# Revit family: FEVH 2 WIDE
name_source: partatom
category: Mechanical Equipment
units: mm (PartAtom-declared; Revit-internal decimal feet)

## family parameters
Always vertical = Yes
Cut with Voids When Loaded = No
Part Type = Normal
Room Calculation Point = No
Round Connector Dimension = Use Diameter
Shared = No
Work Plane-Based = No

## types (6) — shared parameters
Description = 2 Wide Fluid cooler
Fan001 = Yes
Fan002 = Yes
HEIGHT = 90.5 "
Manufacturer = Krack Corporation
Overall Width = 36 "
Revit Family Dates = 9/01/2023HM
Top support visibility = Yes
Type Comments = FEVH * 2 wide fluid cooler (A,C,E, & F )MTR
URL = www.krack.com
WIDTH = 28 "

## per-type parameters (varying)
| type | Copper Pipes | F3 | F4 | F5 | F6 | F7 | Fan003 | Fan004 | Fan005 | Fan006 | Fan007 | LENGTH | Model | Top Support |
| FEH 2X4 | <By Category> | Yes | Yes | No | No | No | Yes | Yes | No | No | No | 220 " | FEH 2 X 4 | Top Support top : F4 |
| FEH 2X5 | <By Category> | Yes | Yes | Yes | No | No | Yes | Yes | Yes | No | No | 274 " | FEH 2 X5 | Top Support top : F5 |
| FEH 2X3 | Copper | Yes | No | No | No | No | Yes | No | No | No | No | 166 " | FEH 2X3 | Top Support top : F3 |
| FEH 2X2 | Copper | No | No | No | No | No | No | No | No | No | No | 112 " | FEH 2 X2 | Top Support top : F2 |
| FEH 2X6 | Copper | Yes | Yes | Yes | Yes | No | Yes | Yes | Yes | Yes | No | 328 " | FEH 2X6 | Top Support top : F6 |
| FEH 2X7 | Copper | Yes | Yes | Yes | Yes | Yes | Yes | Yes | Yes | Yes | Yes | 382 " | FEH 2 X7 | Top Support top : F7 |

## geometry (parser evidence)
native form markers: Sweep x13
no freeform markers — native parametric forms only
